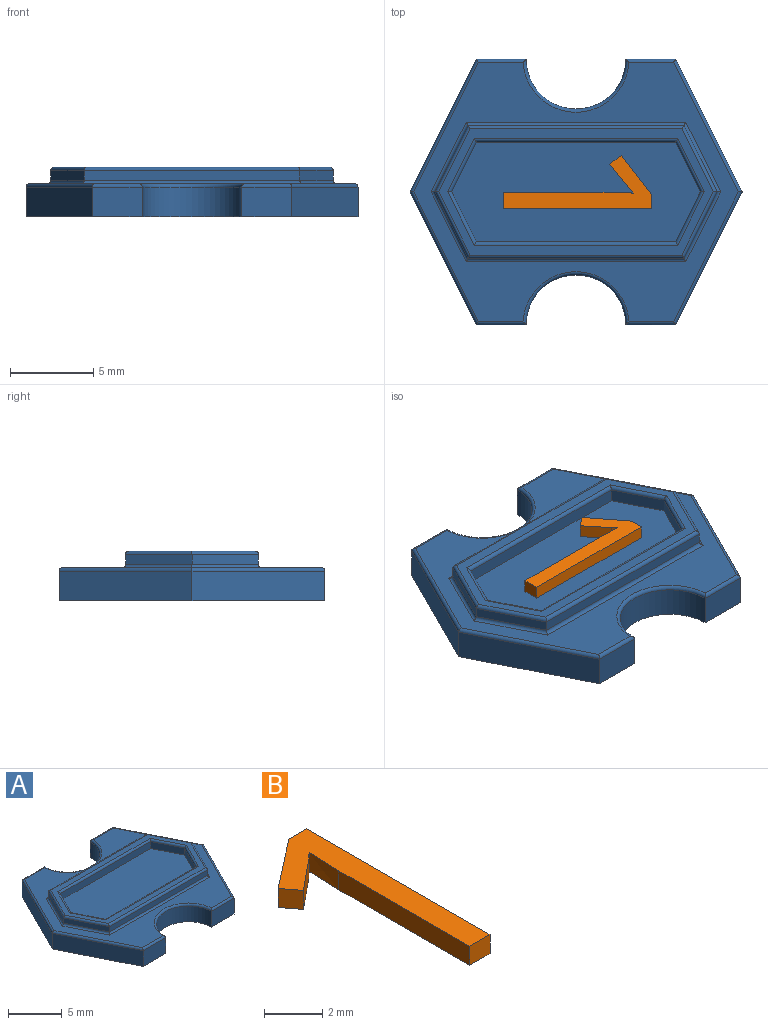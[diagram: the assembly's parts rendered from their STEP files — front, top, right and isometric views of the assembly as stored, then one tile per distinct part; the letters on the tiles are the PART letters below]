
ASSEMBLY  parts=2 mates=1
PART A: 54 faces, bbox 20x16x3 mm
  f0: cylinder r=3mm len=6mm, axis (0,0,-1), area 17mm2, adj f1,f9,f11,f46
  f1: plane 3x1.8mm, normal (0,1,0), area 5.4mm2, adj f0,f2,f11,f44
  f2: plane 8x4mm, normal (-0.89,0.45,0), area 16.1mm2, adj f1,f3,f11,f45
  f3: plane 8x4mm, normal (-0.89,-0.45,0), area 16.1mm2, adj f2,f4,f11,f47
  f4: plane 3x1.8mm, normal (0,-1,0), area 5.4mm2, adj f3,f5,f11,f49
  f5: cylinder r=3mm len=6mm, axis (0,0,-1), area 17mm2, adj f4,f6,f11,f51
  f6: plane 3x1.8mm, normal (0,-1,0), area 5.4mm2, adj f5,f7,f11,f53
  f7: plane 8x4mm, normal (0.89,-0.45,0), area 16.1mm2, adj f6,f8,f11,f52
  f8: plane 8x4mm, normal (0.89,0.45,0), area 16.1mm2, adj f7,f9,f11,f50
  f9: plane 3x1.8mm, normal (0,1,0), area 5.4mm2, adj f0,f8,f11,f48
  f10: plane 19.55x15.6mm, normal (0,0,1), area 85.7mm2, adj f26,f27,f28,f29,f30,f31,f44,f45
  f11: plane 20x16mm, normal (0,0,-1), area 227.7mm2, adj f0,f1,f2,f3,f4,f5,f6,f7
  f12: plane 4x2mm, normal (0.89,0.45,0), area 2.7mm2, adj f13,f23,f28,f40
  f13: plane 13x0.6mm, normal (0,1,0), area 7.8mm2, adj f12,f14,f26,f38
  f14: plane 4x2mm, normal (-0.89,0.45,0), area 2.7mm2, adj f13,f15,f27,f39
  f15: plane 4x2mm, normal (-0.89,-0.45,0), area 2.7mm2, adj f14,f16,f29,f41
  f16: plane 13x0.6mm, normal (0,-1,0), area 7.8mm2, adj f15,f23,f31,f43
  f17: plane 12x0.8mm, normal (0,-1,0), area 9.6mm2, adj f18,f22,f25,f35
  f18: plane 3x1.5mm, normal (-0.89,-0.45,0), area 2.7mm2, adj f17,f19,f25,f37
  f19: plane 3x1.5mm, normal (-0.89,0.45,0), area 2.7mm2, adj f18,f20,f25,f36
  f20: plane 12x0.8mm, normal (0,1,0), area 9.6mm2, adj f19,f21,f25,f34
  f21: plane 3x1.5mm, normal (0.89,0.45,0), area 2.7mm2, adj f20,f22,f25,f32
  f22: plane 3x1.5mm, normal (0.89,-0.45,0), area 2.7mm2, adj f17,f21,f25,f33
  f23: plane 4x2mm, normal (0.89,-0.45,0), area 2.7mm2, adj f12,f16,f30,f42
  f24: plane 16.55x7.6mm, normal (0,0,1), area 22.7mm2, adj f32,f33,f34,f35,f36,f37,f38,f39
  f25: plane 15x6mm, normal (0,0,1), area 81mm2, adj f17,f18,f19,f20,f21,f22
  f26: cylinder r=0.2mm len=13.25mm, axis (-1,0,0), area 4.1mm2, adj f10,f13,f27,f28
  f27: cylinder r=0.2mm len=4.29mm, axis (-0.45,-0.89,0), area 1.4mm2, adj f10,f14,f26,f29
  f28: cylinder r=0.2mm len=4.29mm, axis (-0.45,0.89,0), area 1.4mm2, adj f10,f12,f26,f30
  f29: cylinder r=0.2mm len=4.29mm, axis (0.45,-0.89,0), area 1.4mm2, adj f10,f15,f27,f31
  f30: cylinder r=0.2mm len=4.29mm, axis (0.45,0.89,0), area 1.4mm2, adj f10,f23,f28,f31
  f31: cylinder r=0.2mm len=13.25mm, axis (1,0,0), area 4.1mm2, adj f10,f16,f29,f30
  f32: cylinder r=0.2mm len=3.29mm, axis (0.45,-0.89,0), area 1.1mm2, adj f21,f24,f33,f34
  f33: cylinder r=0.2mm len=3.29mm, axis (-0.45,-0.89,0), area 1.1mm2, adj f22,f24,f32,f35
  f34: cylinder r=0.2mm len=12.25mm, axis (1,0,0), area 3.8mm2, adj f20,f24,f32,f36
  f35: cylinder r=0.2mm len=12.25mm, axis (-1,0,0), area 3.8mm2, adj f17,f24,f33,f37
  f36: cylinder r=0.2mm len=3.29mm, axis (0.45,0.89,0), area 1.1mm2, adj f19,f24,f34,f37
  f37: cylinder r=0.2mm len=3.29mm, axis (-0.45,0.89,0), area 1.1mm2, adj f18,f24,f35,f36
  f38: cylinder r=0.2mm len=13mm, axis (1,0,0), area 4.1mm2, adj f13,f24,f39,f40
  f39: cylinder r=0.2mm len=4.09mm, axis (0.45,0.89,0), area 1.4mm2, adj f14,f24,f38,f41
  f40: cylinder r=0.2mm len=4.09mm, axis (0.45,-0.89,0), area 1.4mm2, adj f12,f24,f38,f42
  f41: cylinder r=0.2mm len=4.09mm, axis (-0.45,0.89,0), area 1.4mm2, adj f15,f24,f39,f43
  f42: cylinder r=0.2mm len=4.09mm, axis (-0.45,-0.89,0), area 1.4mm2, adj f23,f24,f40,f43
  f43: cylinder r=0.2mm len=13mm, axis (-1,0,0), area 4.1mm2, adj f16,f24,f41,f42
  f44: cylinder r=0.2mm len=3mm, axis (1,0,0), area 0.9mm2, adj f1,f10,f45,f46
  f45: cylinder r=0.2mm len=8.09mm, axis (0.45,0.89,0), area 2.8mm2, adj f2,f10,f44,f47
  f46: torus R=3.2mm, axis (0,0,1), area 3mm2, adj f0,f10,f44,f48
  f47: cylinder r=0.2mm len=8.09mm, axis (-0.45,0.89,0), area 2.8mm2, adj f3,f10,f45,f49
  f48: cylinder r=0.2mm len=3mm, axis (1,0,0), area 0.9mm2, adj f9,f10,f46,f50
  f49: cylinder r=0.2mm len=3mm, axis (-1,0,0), area 0.9mm2, adj f4,f10,f47,f51
  f50: cylinder r=0.2mm len=8.09mm, axis (0.45,-0.89,0), area 2.8mm2, adj f8,f10,f48,f52
  f51: torus R=3.2mm, axis (0,0,1), area 3mm2, adj f5,f10,f49,f53
  f52: cylinder r=0.2mm len=8.09mm, axis (-0.45,-0.89,0), area 2.8mm2, adj f7,f10,f50,f53
  f53: cylinder r=0.2mm len=3mm, axis (-1,0,0), area 0.9mm2, adj f6,f10,f51,f52
PART B: 11 faces, bbox 3.2x8.9x0.8 mm
  f0: plane 0.99x0.8mm, normal (0,-1,0), area 0.8mm2, adj f1,f8,f9,f10
  f1: plane 8.92x0.8mm, normal (1,0,0), area 7.1mm2, adj f0,f2,f9,f10
  f2: plane 0.85x0.8mm, normal (0,1,0), area 0.7mm2, adj f1,f3,f9,f10
  f3: plane 2.36x1.83mm, normal (-0.61,0.79,0), area 2.4mm2, adj f2,f4,f9,f10
  f4: plane 0.8x0.7mm, normal (-0.79,-0.61,0), area 0.7mm2, adj f3,f5,f9,f10
  f5: extruded ~1.45x1.19mm, area 1.5mm2, adj f4,f6,f9,f10
  f6: extruded ~0.8x0.29mm, area 0.3mm2, adj f5,f7,f9,f10
  f7: extruded ~1.5x0.8mm, area 1.2mm2, adj f6,f8,f9,f10
  f8: plane 6.36x0.8mm, normal (-1,0,0), area 5.1mm2, adj f0,f7,f9,f10
  f9: plane 8.92x3.22mm, normal (0,0,1), area 10.9mm2, adj f0,f1,f2,f3,f4,f5,f6,f7
  f10: plane 8.92x3.22mm, normal (0,0,-1), area 10.9mm2, adj f0,f1,f2,f3,f4,f5,f6,f7
PLACE A at identity
PLACE B rot(axis=(0,0,-1),90deg) t=(0.25,0.77,2)mm
MATE parallel B.f10 <-> A.f25  axis (0,0,-1) through (0.68,-0.23,2)mm
